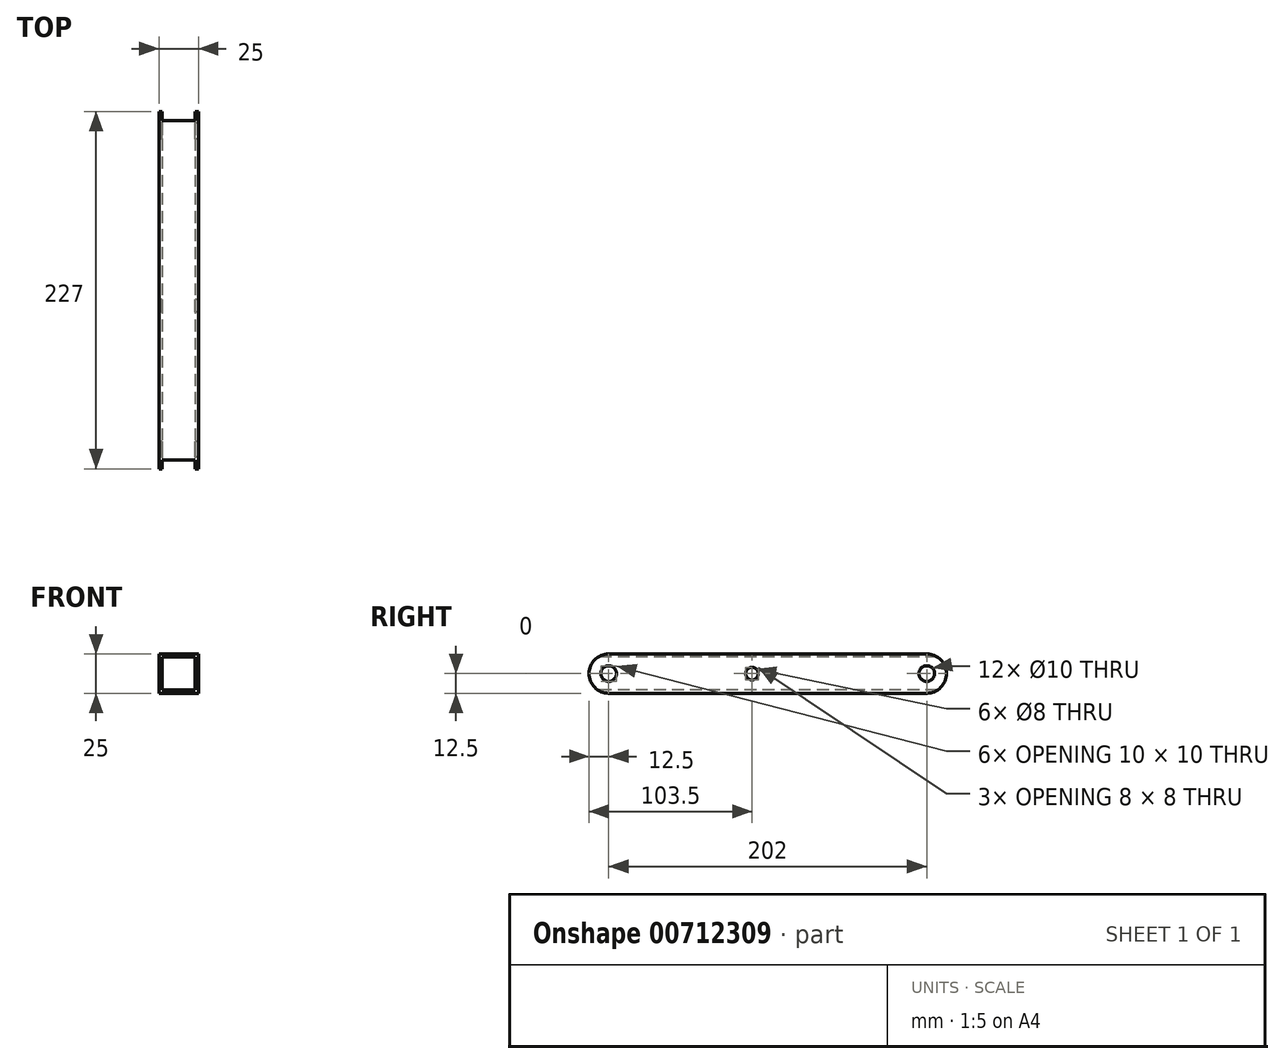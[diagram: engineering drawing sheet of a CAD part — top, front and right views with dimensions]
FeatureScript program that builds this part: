
annotation { "Feature Type Name" : "Feature", "Feature Type Description" : "" }
export const myFeature = defineFeature(function(context is Context, id is Id, definition is map)
    precondition{}
    {
        {
            var Q0;
            Q0=qCreatedBy(makeId("Right.planeOp"),FACE);
            var sketch = newSketch(context, id + "F0", { "sketchPlane" : qUnion([Q0])});
            skLineSegment(sketch, "E0.bottom", {"start": v(101, 12.5) * mm, "end": v(-101, 12.5) * mm});
            skLineSegment(sketch, "E0.top", {"start": v(101, -12.5) * mm, "end": v(-101, -12.5) * mm});
            skLineSegment(sketch, "E0.left", {"start": v(101, 12.5) * mm, "end": v(101, -12.5) * mm, "construction": true});
            skLineSegment(sketch, "E0.right", {"start": v(-101, 12.5) * mm, "end": v(-101, -12.5) * mm, "construction": true});
            skPoint(sketch, "E0.middle", {"position": v(0, 0) * mm});
            skCircle(sketch, "E1", {"center": v(-10, 0) * mm, "radius": 4 * mm});
            skArc(sketch, "E2", {"start": v(-101, 12.5) * mm, "mid": v(-113.5, 0) * mm, "end": v(-101, -12.5) * mm});
            skArc(sketch, "E3", {"start": v(101, 12.5) * mm, "mid": v(113.5, 0) * mm, "end": v(101, -12.5) * mm});
            skCircle(sketch, "E4", {"center": v(-101, 0) * mm, "radius": 5 * mm});
            skCircle(sketch, "E5", {"center": v(101, 0) * mm, "radius": 5 * mm});
            skSolve(sketch);
        }
        {
            var Q0;
            Q0 = qSketchRegion(id + "F0", true);
            extrude(context, id + "F1", {"entities" : qUnion([Q0]), "depth" : 25 * mm, "offsetDistance" : 25 * mm});
        }
        {
            var Q0;
            Q0=qCreatedBy(makeId("Front.planeOp"),FACE);
            var sketch = newSketch(context, id + "F2", { "sketchPlane" : qUnion([Q0])});
            skLineSegment(sketch, "E6.0", {"start": v(2, 10.5) * mm, "end": v(2, -10.5) * mm});
            skLineSegment(sketch, "E6.1", {"start": v(23, 10.5) * mm, "end": v(2, 10.5) * mm});
            skLineSegment(sketch, "E6.2", {"start": v(23, 10.5) * mm, "end": v(23, -10.5) * mm});
            skLineSegment(sketch, "E6.3", {"start": v(23, -10.5) * mm, "end": v(2, -10.5) * mm});
            skSolve(sketch);
        }
        {
            var Q0;
            Q0 = qSketchRegion(id + "F2", true);
            extrude(context, id + "F3", {"entities" : qUnion([Q0]), "operationType" : NewBodyOperationType.REMOVE, "endBound" : BoundingType.THROUGH_ALL, "oppositeDirection" : true, "depth" : 25 * mm, "offsetDistance" : 25 * mm, "hasSecondDirection" : true, "secondDirectionBound" : BoundingType.THROUGH_ALL, "secondDirectionOppositeDirection" : false, "secondDirectionDepth" : 25 * mm});
        }
    });
